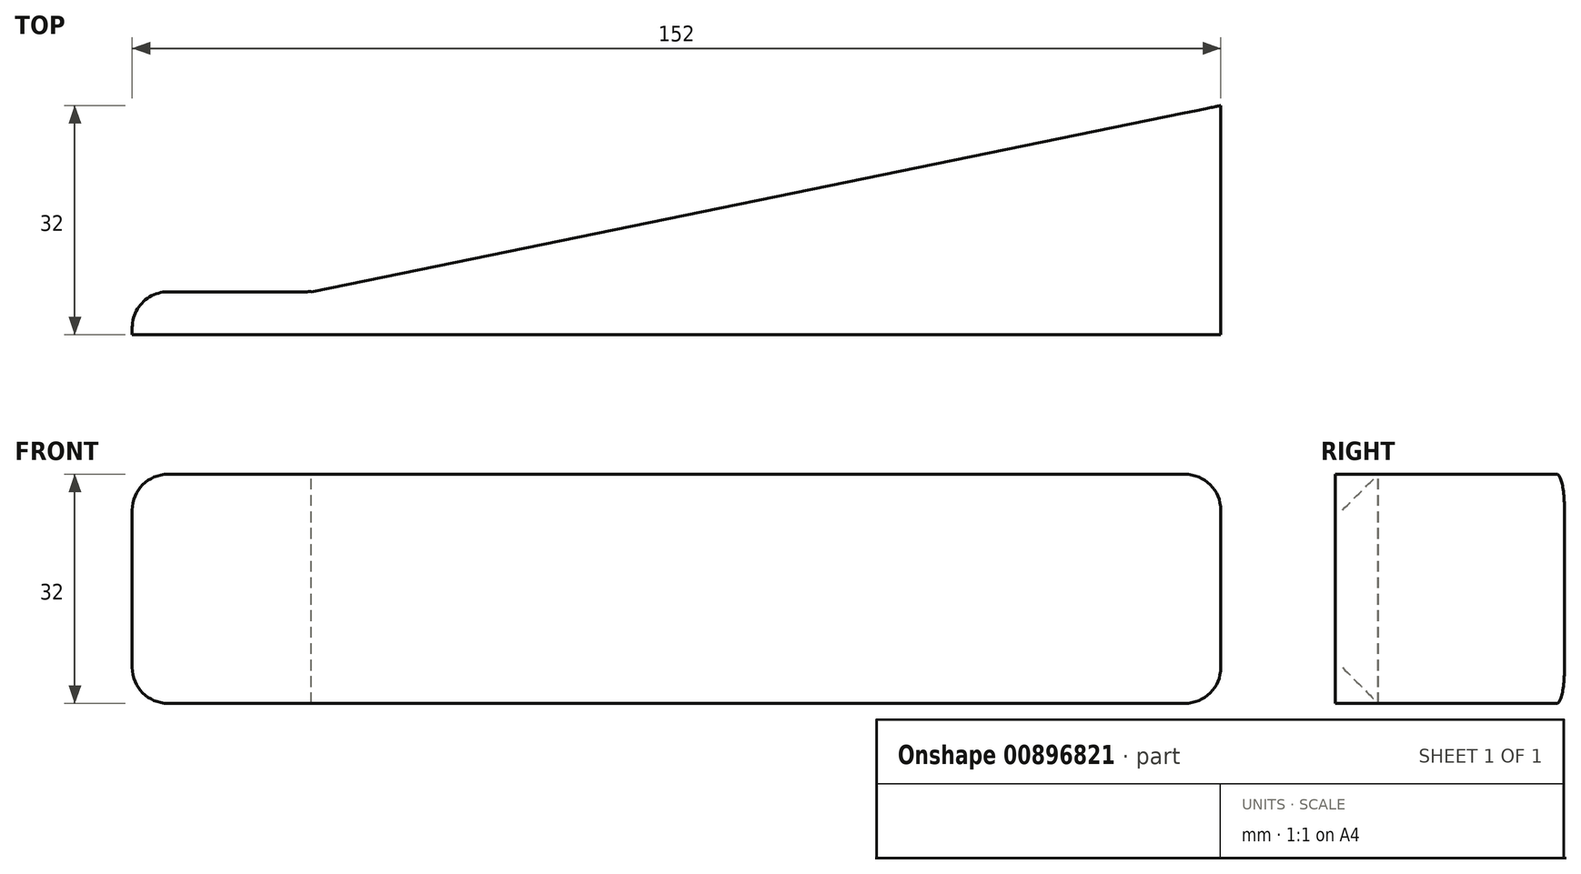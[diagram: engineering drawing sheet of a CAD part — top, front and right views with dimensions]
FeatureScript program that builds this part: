
annotation { "Feature Type Name" : "Feature", "Feature Type Description" : "" }
export const myFeature = defineFeature(function(context is Context, id is Id, definition is map)
    precondition{}
    {
        {
            var Q0;
            Q0=qCreatedBy(makeId("Top.planeOp"),FACE);
            var sketch = newSketch(context, id + "F0", { "sketchPlane" : qUnion([Q0])});
            skLineSegment(sketch, "E0.bottom", {"start": v(63.5, 16) * mm, "end": v(-63.5, 16) * mm});
            skLineSegment(sketch, "E0.top", {"start": v(63.5, -16) * mm, "end": v(-63.5, -16) * mm});
            skLineSegment(sketch, "E0.left", {"start": v(63.5, 16) * mm, "end": v(63.5, -16) * mm});
            skLineSegment(sketch, "E0.right", {"start": v(-63.5, 16) * mm, "end": v(-63.5, -16) * mm});
            skPoint(sketch, "E0.middle", {"position": v(0, 0) * mm});
            skSolve(sketch);
        }
        {
            var Q0;
            Q0 = qSketchRegion(id + "F0", true);
            extrude(context, id + "F1", {"entities" : qUnion([Q0]), "depth" : 32 * mm, "offsetDistance" : 25 * mm});
        }
        {
            var Q0;
            Q0=makeQuery(id+"F1.opExtrude","CAP_FACE",FACE,{"disambiguationData":[OSD([sQuery(id+"F0.wireOp",EDGE,"E0.bottom"),sQuery(id+"F0.wireOp",EDGE,"E0.top"),sQuery(id+"F0.wireOp",EDGE,"E0.left"),sQuery(id+"F0.wireOp",EDGE,"E0.right")])],"isStart":false});
            var sketch = newSketch(context, id + "F2", { "sketchPlane" : qUnion([Q0])});
            skLineSegment(sketch, "E1", {"start": v(-63.5, -16) * mm, "end": v(-63.5, -10) * mm});
            skLineSegment(sketch, "E2", {"start": v(-63.5, -10) * mm, "end": v(63.5, 16) * mm});
            skSolve(sketch);
        }
        {
            var Q0;
            {var subQ0=sQuery(id+"F2.wireOp",EDGE,"E2");Q0=makeQuery(id+"F2.imprint","IMPRINT",FACE,{"disambiguationData":[TD([[makeQuery(id+"F2.imprint","IMPRINT",EDGE,{"derivedFrom":subQ0}),1.0]])]});}
            extrude(context, id + "F3", {"entities" : qUnion([Q0]), "operationType" : NewBodyOperationType.REMOVE, "endBound" : BoundingType.UP_TO_NEXT, "oppositeDirection" : true, "depth" : 32 * mm, "offsetDistance" : 25 * mm});
        }
        {
            var Q0;
            Q0=makeQuery(id+"F1.opExtrude","SWEPT_FACE",FACE,{"disambiguationData":[OSD([sQuery(id+"F0.wireOp",EDGE,"E0.right")])]});
            extrude(context, id + "F4", {"entities" : qUnion([Q0]), "operationType" : NewBodyOperationType.ADD, "depth" : 25 * mm, "offsetDistance" : 25 * mm});
        }
        {
            var Q0;
            Q0=makeQuery(id+"F1.opExtrude","CAP_EDGE",EDGE,{"disambiguationData":[OSD([sQuery(id+"F0.wireOp",EDGE,"E0.left")])],"isStart":false});
            var Q1;
            Q1=makeQuery(id+"F1.opExtrude","CAP_EDGE",EDGE,{"disambiguationData":[OSD([sQuery(id+"F0.wireOp",EDGE,"E0.left")])],"isStart":true});
            var Q2;
            {var subQ0=sQuery(id+"F2.wireOp",EDGE,"E2");var subQ1=sQuery(id+"F2.wireOp",EDGE,"E1");var subQ2=sQuery(id+"F0.wireOp",EDGE,"E0.right");Q2=makeQuery(id+"F4.boolean.opBoolean","MERGE",EDGE,{"derivedFrom":[makeQuery(id+"F3.boolean.opBoolean","COPY",EDGE,{"derivedFrom":makeQuery(id+"F3.opExtrude","SWEPT_EDGE",EDGE,{"disambiguationData":[OSD([subQ2,subQ1,subQ0])]})}),makeQuery(id+"F4.opExtrude","CAP_EDGE",EDGE,{"disambiguationData":[OSD([subQ2,subQ1,subQ0])],"isStart":true})]});}
            var Q3;
            Q3=makeQuery(id+"F4.opExtrude","CAP_EDGE",EDGE,{"disambiguationData":[OSD([sQuery(id+"F0.wireOp",EDGE,"E0.right"),sQuery(id+"F2.wireOp",EDGE,"E1"),sQuery(id+"F2.wireOp",EDGE,"E2")])],"isStart":false});
            var Q4;
            {var subQ0=sQuery(id+"F0.wireOp",EDGE,"E0.right");Q4=makeQuery(id+"F4.opExtrude","CAP_EDGE",EDGE,{"disambiguationData":[OSD([subQ0]),TDD([makeQuery(id+"F1.opExtrude","CAP_EDGE",EDGE,{"disambiguationData":[OSD([subQ0])],"isStart":false})])],"isStart":false});}
            var Q5;
            {var subQ0=sQuery(id+"F0.wireOp",EDGE,"E0.right");Q5=makeQuery(id+"F4.opExtrude","CAP_EDGE",EDGE,{"disambiguationData":[OSD([subQ0]),TDD([makeQuery(id+"F1.opExtrude","CAP_EDGE",EDGE,{"disambiguationData":[OSD([subQ0])],"isStart":true})])],"isStart":false});}
            fillet(context, id + "F5", {"entities" : qUnion([Q0, Q1, Q2, Q3, Q4, Q5]), "radius" : 5 * mm, "tangentPropagation" : true, "allowEdgeOverflow" : false});
        }
    });
